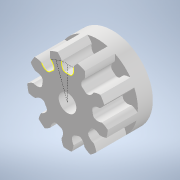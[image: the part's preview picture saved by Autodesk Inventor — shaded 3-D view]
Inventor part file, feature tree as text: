
AUTODESK INVENTOR PART (.ipt)
format: ipt  version: 2022 (Build 260153070, 153G)  size: 411,648 bytes
history: native  units: mm
features: extrude x5, sketch x4, pattern_circular x1
ambient origin geometry x8: Origin, YZ Plane, XZ Plane, XY Plane, X Axis, Y Axis, Z Axis, Center Point
bodies: Solid1 (feature_tree)
feature tree (10):
  sketch  "Sketch1"  dims[d0=3.0mm d1=0.0mm]
  extrude  "Extrusion1"  TaperAngle=0.0deg  [1 undecoded]
  extrude  "Extrusion2"  Depth=90.0mm TaperAngle=360.0deg
  pattern_circular  "Circular Pattern1"  [2 undecoded]
  sketch  "Sketch2"  dims[d2=10.0mm d3=0.0mm d4=90.0mm d5=360.0deg]
  extrude  "Extrusion3"  Depth=6.1mm
  extrude  "Extrusion4"  Depth=2.0mm TaperAngle=0.0deg
  extrude  "Extrusion5"  [1 undecoded]
  sketch  "Sketch3"  dims[d7=2.35mm]
  sketch  "Sketch5"  dims[d8=3.0mm d9=0.0mm d10=1.0mm d11=0.0mm d12=6.1mm d14=2.0mm d15=0.0mm]
note: 4 required parameter values undecoded (feature->parameter linkage not recoverable at this tier; creation-order binding heuristic only, values carry confidence <= 0.55)
